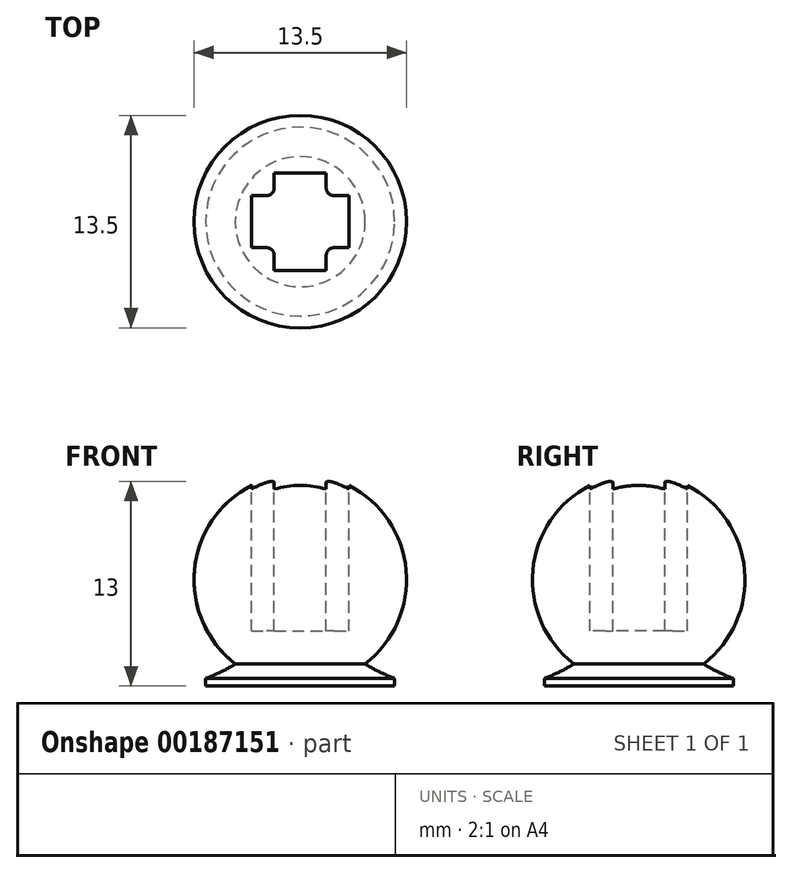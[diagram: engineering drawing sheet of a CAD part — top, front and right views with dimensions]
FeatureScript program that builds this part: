
annotation { "Feature Type Name" : "Feature", "Feature Type Description" : "" }
export const myFeature = defineFeature(function(context is Context, id is Id, definition is map)
    precondition{}
    {
        {
            var Q0;
            Q0=qCreatedBy(makeId("Front.planeOp"),FACE);
            var sketch = newSketch(context, id + "F0", { "sketchPlane" : qUnion([Q0])});
            skArc(sketch, "E0", {"start": v(0, -13.5) * mm, "mid": v(6.75, -6.75) * mm, "end": v(0, 0) * mm});
            skLineSegment(sketch, "E1", {"start": v(0, 0) * mm, "end": v(0, -13.5) * mm});
            skSolve(sketch);
        }
        {
            var Q0;
            Q0=makeQuery(id+"F0.imprint","IMPRINT",FACE,{"disambiguationData":[TD([[makeQuery(id+"F0.imprint","IMPRINT",EDGE,{"derivedFrom":sQuery(id+"F0.wireOp",EDGE,"E0")}),1.0]])]});
            var Q1;
            Q1=sQuery(id+"F0.wireOp",EDGE,"E1");
            revolve(context, id + "F1", {"entities" : qUnion([Q0]), "axis" : qUnion([Q1]), "revolveType" : RevolveType.FULL});
        }
        {
            var Q0;
            Q0=qCreatedBy(makeId("Top.planeOp"),FACE);
            var sketch = newSketch(context, id + "F2", { "sketchPlane" : qUnion([Q0])});
            skLineSegment(sketch, "E2", {"start": v(0, 0) * mm, "end": v(-3.1, 0) * mm, "construction": true});
            skLineSegment(sketch, "E3", {"start": v(-3.1, 0) * mm, "end": v(-3.1, -1.65) * mm});
            skLineSegment(sketch, "E4", {"start": v(-3.1, -1.65) * mm, "end": v(-2.15, -1.65) * mm});
            skLineSegment(sketch, "E5", {"start": v(-1.65, -2.15) * mm, "end": v(-1.65, -3.1) * mm});
            skLineSegment(sketch, "E6", {"start": v(-1.65, -3.1) * mm, "end": v(0, -3.1) * mm});
            skLineSegment(sketch, "E7", {"start": v(0, -3.1) * mm, "end": v(0, 0) * mm, "construction": true});
            skPoint(sketch, "E8.visualSharp", {"position": v(-1.65, -1.65) * mm});
            skArc(sketch, "E8.filletArc", {"start": v(-1.65, -2.15) * mm, "mid": v(-1.8, -1.8) * mm, "end": v(-2.15, -1.65) * mm});
            skLineSegment(sketch, "E9.1.0", {"start": v(0, -3.1) * mm, "end": v(1.65, -3.1) * mm});
            skLineSegment(sketch, "E9.1.1", {"start": v(1.65, -3.1) * mm, "end": v(1.65, -2.15) * mm});
            skArc(sketch, "E9.1.2", {"start": v(2.15, -1.65) * mm, "mid": v(1.8, -1.8) * mm, "end": v(1.65, -2.15) * mm});
            skLineSegment(sketch, "E9.1.3", {"start": v(2.15, -1.65) * mm, "end": v(3.1, -1.65) * mm});
            skLineSegment(sketch, "E9.1.4", {"start": v(3.1, -1.65) * mm, "end": v(3.1, 0) * mm});
            skLineSegment(sketch, "E9.2.0", {"start": v(3.1, 0) * mm, "end": v(3.1, 1.65) * mm});
            skLineSegment(sketch, "E9.2.1", {"start": v(3.1, 1.65) * mm, "end": v(2.15, 1.65) * mm});
            skArc(sketch, "E9.2.2", {"start": v(1.65, 2.15) * mm, "mid": v(1.8, 1.8) * mm, "end": v(2.15, 1.65) * mm});
            skLineSegment(sketch, "E9.2.3", {"start": v(1.65, 2.15) * mm, "end": v(1.65, 3.1) * mm});
            skLineSegment(sketch, "E9.2.4", {"start": v(1.65, 3.1) * mm, "end": v(0, 3.1) * mm});
            skLineSegment(sketch, "E9.3.0", {"start": v(0, 3.1) * mm, "end": v(-1.65, 3.1) * mm});
            skLineSegment(sketch, "E9.3.1", {"start": v(-1.65, 3.1) * mm, "end": v(-1.65, 2.15) * mm});
            skArc(sketch, "E9.3.2", {"start": v(-2.15, 1.65) * mm, "mid": v(-1.8, 1.8) * mm, "end": v(-1.65, 2.15) * mm});
            skLineSegment(sketch, "E9.3.3", {"start": v(-2.15, 1.65) * mm, "end": v(-3.1, 1.65) * mm});
            skLineSegment(sketch, "E9.3.4", {"start": v(-3.1, 1.65) * mm, "end": v(-3.1, 0) * mm});
            skPoint(sketch, "E9.center", {"position": v(0, 0) * mm});
            skSolve(sketch);
        }
        {
            var Q0;
            Q0 = qSketchRegion(id + "F2", true);
            extrude(context, id + "F3", {"entities" : qUnion([Q0]), "operationType" : NewBodyOperationType.REMOVE, "oppositeDirection" : true, "depth" : 10 * mm});
        }
        {
            var Q0;
            Q0=qCreatedBy(makeId("Front.planeOp"),FACE);
            var sketch = newSketch(context, id + "F4", { "sketchPlane" : qUnion([Q0])});
            skArc(sketch, "E10", {"start": v(-2.6, -0.52) * mm, "mid": v(0, -13.5) * mm, "end": v(2.6, -0.52) * mm, "construction": true});
            skLineSegment(sketch, "E11", {"start": v(-6, -13.5) * mm, "end": v(0, -13.5) * mm});
            skArc(sketch, "E12", {"start": v(-6, -13) * mm, "mid": v(-5.04, -12.6) * mm, "end": v(-4.13, -12.1) * mm});
            skLineSegment(sketch, "E13", {"start": v(0, -12.1) * mm, "end": v(0, -13.5) * mm});
            skPoint(sketch, "E14.orphan", {"position": v(6, -13.5) * mm});
            skLineSegment(sketch, "E15", {"start": v(0, -13.5) * mm, "end": v(0, -12.1) * mm});
            skLineSegment(sketch, "E16", {"start": v(-4.13, -12.1) * mm, "end": v(0, -12.1) * mm});
            skPoint(sketch, "E17.orphan", {"position": v(0, -4.55) * mm});
            skLineSegment(sketch, "E18", {"start": v(-6, -13) * mm, "end": v(-6, -13.5) * mm});
            skSolve(sketch);
        }
        {
            var Q0;
            Q0=makeQuery(id+"F4.imprint","IMPRINT",FACE,{"disambiguationData":[TD([[makeQuery(id+"F4.imprint","IMPRINT",EDGE,{"derivedFrom":sQuery(id+"F4.wireOp",EDGE,"E11")}),1.0]])]});
            var Q1;
            Q1=sQuery(id+"F4.wireOp",EDGE,"E15");
            revolve(context, id + "F5", {"operationType" : NewBodyOperationType.ADD, "entities" : qUnion([Q0]), "axis" : qUnion([Q1]), "revolveType" : RevolveType.FULL});
        }
    });
